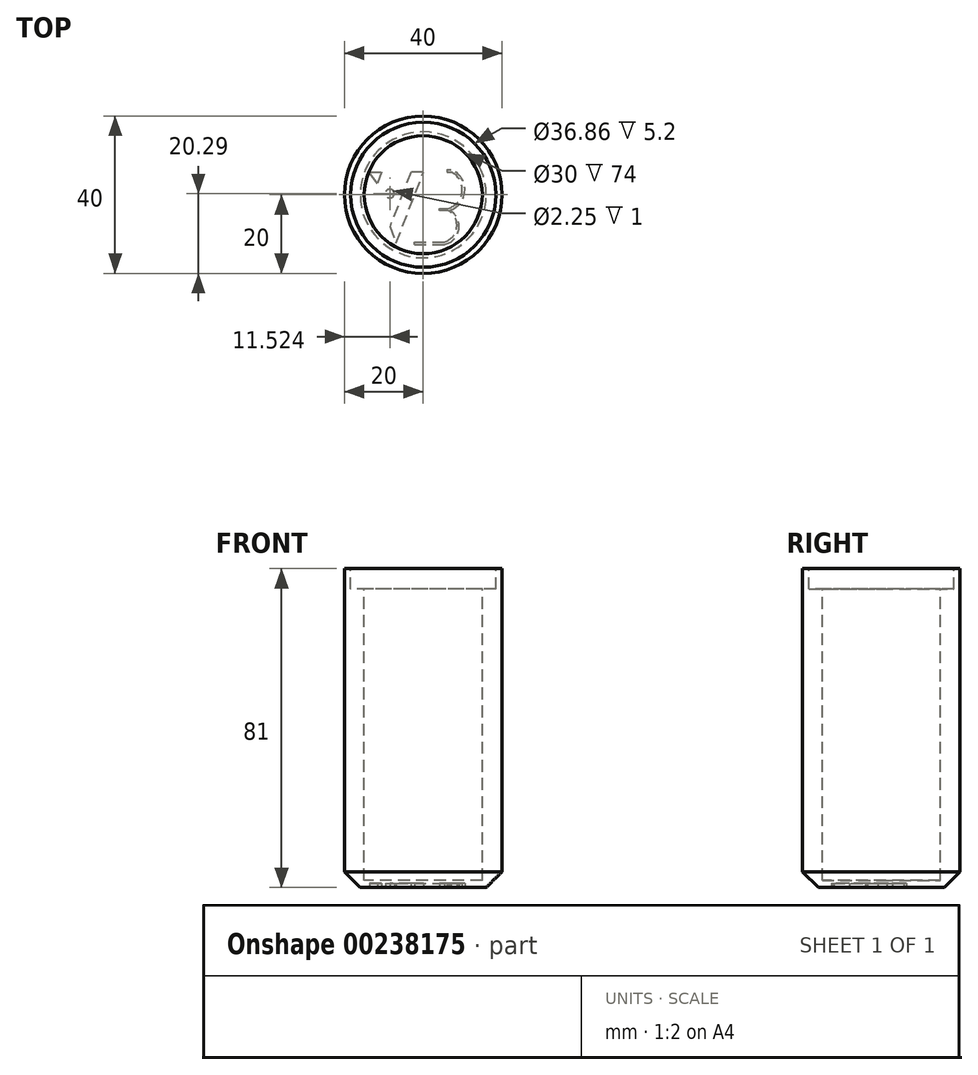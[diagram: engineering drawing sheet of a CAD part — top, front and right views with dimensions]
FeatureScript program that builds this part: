
annotation { "Feature Type Name" : "Feature", "Feature Type Description" : "" }
export const myFeature = defineFeature(function(context is Context, id is Id, definition is map)
    precondition{}
    {
        {
            var Q0;
            Q0=qCreatedBy(makeId("Top.planeOp"),FACE);
            var sketch = newSketch(context, id + "F0", { "sketchPlane" : qUnion([Q0])});
            skCircle(sketch, "E0", {"center": v(0, 0) * mm, "radius": 20 * mm});
            skSolve(sketch);
        }
        {
            var Q0;
            Q0=makeQuery(id+"F0.imprint","IMPRINT",FACE,{"disambiguationData":[TD([[makeQuery(id+"F0.imprint","IMPRINT",EDGE,{"derivedFrom":sQuery(id+"F0.wireOp",EDGE,"E0")}),1.0]])]});
            extrude(context, id + "F1", {"entities" : qUnion([Q0]), "depth" : 81 * mm, "offsetDistance" : 25 * mm});
        }
        {
            var Q0;
            Q0=makeQuery(id+"F1.opExtrude","CAP_FACE",FACE,{"disambiguationData":[OSD([sQuery(id+"F0.wireOp",EDGE,"E0")])],"isStart":false});
            var sketch = newSketch(context, id + "F2", { "sketchPlane" : qUnion([Q0])});
            skCircle(sketch, "E1", {"center": v(0, 0) * mm, "radius": 18.43 * mm});
            skSolve(sketch);
        }
        {
            var Q0;
            Q0=makeQuery(id+"F2.imprint","IMPRINT",FACE,{"disambiguationData":[TD([[makeQuery(id+"F2.imprint","IMPRINT",EDGE,{"derivedFrom":sQuery(id+"F2.wireOp",EDGE,"E1")}),1.0]])]});
            extrude(context, id + "F3", {"entities" : qUnion([Q0]), "operationType" : NewBodyOperationType.REMOVE, "oppositeDirection" : true, "depth" : 5.2 * mm, "offsetDistance" : 25 * mm});
        }
        {
            var Q0;
            Q0=makeQuery(id+"F3.boolean.opBoolean","COPY",FACE,{"derivedFrom":makeQuery(id+"F3.opExtrude","CAP_FACE",FACE,{"disambiguationData":[OSD([sQuery(id+"F2.wireOp",EDGE,"E1")])],"isStart":false})});
            var sketch = newSketch(context, id + "F4", { "sketchPlane" : qUnion([Q0])});
            skCircle(sketch, "E2", {"center": v(0, 0) * mm, "radius": 15 * mm});
            skSolve(sketch);
        }
        {
            var Q0;
            Q0=makeQuery(id+"F4.imprint","IMPRINT",FACE,{"disambiguationData":[TD([[makeQuery(id+"F4.imprint","IMPRINT",EDGE,{"derivedFrom":sQuery(id+"F4.wireOp",EDGE,"E2")}),1.0]])]});
            extrude(context, id + "F5", {"entities" : qUnion([Q0]), "operationType" : NewBodyOperationType.REMOVE, "oppositeDirection" : true, "depth" : 74 * mm, "offsetDistance" : 25 * mm});
        }
        {
            var Q0;
            Q0=makeQuery(id+"F1.opExtrude","CAP_EDGE",EDGE,{"disambiguationData":[OSD([sQuery(id+"F0.wireOp",EDGE,"E0")])],"isStart":true});
            chamfer(context, id + "F6", {"entities" : qUnion([Q0]), "width" : 4 * mm, "tangentPropagation" : true});
        }
        {
            var Q0;
            Q0=makeQuery(id+"F1.opExtrude","CAP_FACE",FACE,{"disambiguationData":[OSD([sQuery(id+"F0.wireOp",EDGE,"E0")])],"isStart":true});
            var sketch = newSketch(context, id + "F7", { "sketchPlane" : qUnion([Q0])});
            skLineSegment(sketch, "E3", {"start": v(-13.7, -5.74) * mm, "end": v(-10.55, -5.74) * mm});
            skLineSegment(sketch, "E4", {"start": v(-10.55, -5.74) * mm, "end": v(-11.64, -2.85) * mm});
            skLineSegment(sketch, "E5", {"start": v(-11.64, -2.85) * mm, "end": v(-13.7, -5.74) * mm});
            skCircle(sketch, "E6", {"center": v(-8.48, -0.29) * mm, "radius": 1.13 * mm});
            skLineSegment(sketch, "E7", {"start": v(-8.47, 8.02) * mm, "end": v(-6.87, 12.29) * mm});
            skLineSegment(sketch, "E8", {"start": v(-6.87, 12.29) * mm, "end": v(0.01, -5.73) * mm});
            skLineSegment(sketch, "E9", {"start": v(0.01, -5.73) * mm, "end": v(-3.12, -5.73) * mm});
            skLineSegment(sketch, "E10", {"start": v(-3.12, -5.73) * mm, "end": v(-8.47, 8.02) * mm});
            skSolve(sketch);
        }
        {
            var Q0;
            Q0=makeQuery(id+"F7.imprint","IMPRINT",FACE,{"disambiguationData":[TD([[makeQuery(id+"F7.imprint","IMPRINT",EDGE,{"derivedFrom":sQuery(id+"F7.wireOp",EDGE,"E7")}),-1.0]])]});
            var Q1;
            Q1=makeQuery(id+"F7.imprint","IMPRINT",FACE,{"disambiguationData":[TD([[makeQuery(id+"F7.imprint","IMPRINT",EDGE,{"derivedFrom":sQuery(id+"F7.wireOp",EDGE,"E6")}),1.0]])]});
            var Q2;
            Q2=makeQuery(id+"F7.imprint","IMPRINT",FACE,{"disambiguationData":[TD([[makeQuery(id+"F7.imprint","IMPRINT",EDGE,{"derivedFrom":sQuery(id+"F7.wireOp",EDGE,"E3")}),1.0]])]});
            extrude(context, id + "F8", {"entities" : qUnion([Q0, Q1, Q2]), "operationType" : NewBodyOperationType.REMOVE, "oppositeDirection" : true, "depth" : 1 * mm, "offsetDistance" : 25 * mm});
        }
        {
            var Q0;
            Q0=makeQuery(id+"F1.opExtrude","CAP_FACE",FACE,{"disambiguationData":[OSD([sQuery(id+"F0.wireOp",EDGE,"E0")])],"isStart":true});
            var sketch = newSketch(context, id + "F9", { "sketchPlane" : qUnion([Q0])});
            skLineSegment(sketch, "E11", {"start": v(-2.24, 12.65) * mm, "end": v(5.37, 12.65) * mm});
            skLineSegment(sketch, "E12", {"start": v(-2.24, 12.65) * mm, "end": v(-2.24, 11.97) * mm});
            skLineSegment(sketch, "E13", {"start": v(-2.24, 11.97) * mm, "end": v(5.4, 11.97) * mm});
            skLineSegment(sketch, "E14", {"start": v(6.31, 3.96) * mm, "end": v(4.14, 3.96) * mm});
            skLineSegment(sketch, "E15", {"start": v(4.14, 3.96) * mm, "end": v(4.14, 3.5) * mm});
            skLineSegment(sketch, "E16", {"start": v(4.14, 3.5) * mm, "end": v(6.31, 3.5) * mm});
            skArc(sketch, "E17", {"start": v(6.31, 3.96) * mm, "mid": v(8.5, 8.27) * mm, "end": v(5.4, 11.97) * mm});
            skArc(sketch, "E18", {"start": v(6.78, 3.96) * mm, "mid": v(9.05, 8.79) * mm, "end": v(5.37, 12.65) * mm});
            skLineSegment(sketch, "E19", {"start": v(6, -6.44) * mm, "end": v(6, -5.8) * mm});
            skLineSegment(sketch, "E20", {"start": v(6, -5.8) * mm, "end": v(7.03, -5.8) * mm});
            skLineSegment(sketch, "E21", {"start": v(6, -6.44) * mm, "end": v(7.07, -6.44) * mm});
            skArc(sketch, "E22", {"start": v(7.03, -5.8) * mm, "mid": v(9.9, -0.9) * mm, "end": v(6.31, 3.5) * mm});
            skArc(sketch, "E23", {"start": v(7.07, -6.44) * mm, "mid": v(10.56, -1.13) * mm, "end": v(6.78, 3.96) * mm});
            skSolve(sketch);
        }
        {
            var Q0;
            Q0=makeQuery(id+"F9.imprint","IMPRINT",FACE,{"disambiguationData":[TD([[makeQuery(id+"F9.imprint","IMPRINT",EDGE,{"derivedFrom":sQuery(id+"F9.wireOp",EDGE,"E11")}),-1.0]])]});
            extrude(context, id + "F10", {"entities" : qUnion([Q0]), "operationType" : NewBodyOperationType.REMOVE, "oppositeDirection" : true, "depth" : 1 * mm, "offsetDistance" : 25 * mm});
        }
    });
